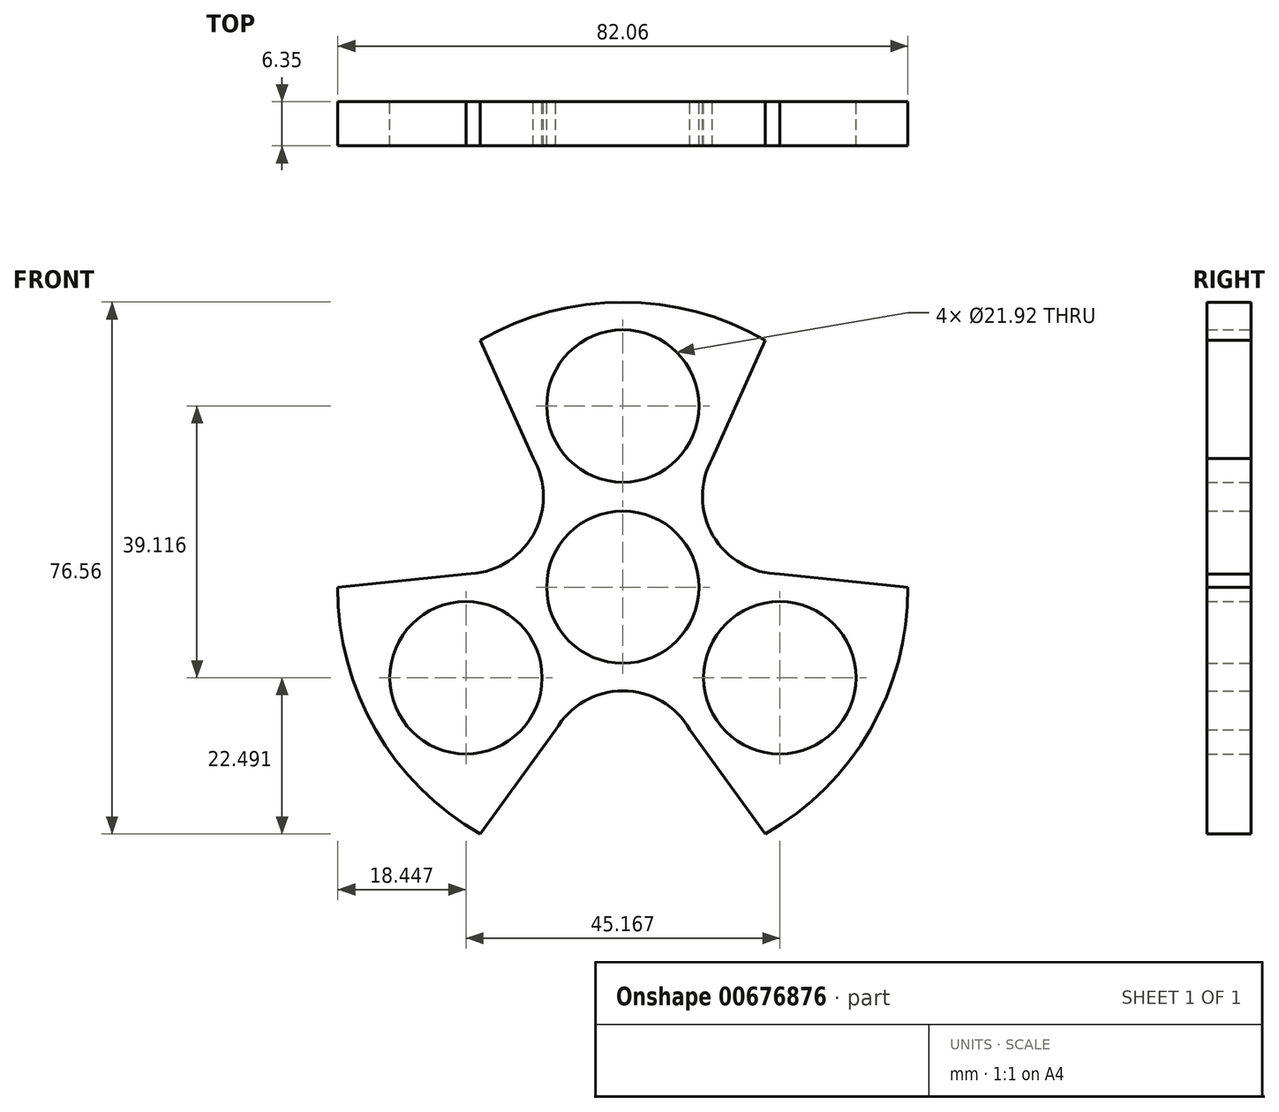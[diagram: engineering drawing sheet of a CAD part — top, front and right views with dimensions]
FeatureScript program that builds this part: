
annotation { "Feature Type Name" : "Feature", "Feature Type Description" : "" }
export const myFeature = defineFeature(function(context is Context, id is Id, definition is map)
    precondition{}
    {
        {
            var Q0;
            Q0=qCreatedBy(makeId("Front.planeOp"),FACE);
            var sketch = newSketch(context, id + "F0", { "sketchPlane" : qUnion([Q0])});
            skCircle(sketch, "E0", {"center": v(0, 0) * mm, "radius": 10.96 * mm});
            skCircle(sketch, "E1.cCircle", {"center": v(0, 0) * mm, "radius": 22.58 * mm, "construction": true});
            skPoint(sketch, "E1.0.midPoint", {"position": v(22.58, 0) * mm});
            skCircle(sketch, "E2", {"center": v(22.58, -13.04) * mm, "radius": 10.96 * mm});
            skPoint(sketch, "E2.perimeterSnap0", {"position": v(11.3, -19.56) * mm});
            skCircle(sketch, "E3", {"center": v(-22.58, -13.04) * mm, "radius": 10.96 * mm});
            skCircle(sketch, "E4", {"center": v(0, 26.08) * mm, "radius": 10.96 * mm});
            skArc(sketch, "E5", {"start": v(-22.58, 1.9) * mm, "mid": v(-12.94, 7.47) * mm, "end": v(-12.94, 18.6) * mm});
            skArc(sketch, "E6", {"start": v(12.9, 18.54) * mm, "mid": v(12.96, 7.43) * mm, "end": v(22.58, 1.9) * mm});
            skArc(sketch, "E7", {"start": v(9.65, -20.5) * mm, "mid": v(0, -14.94) * mm, "end": v(-9.65, -20.5) * mm});
            skCircle(sketch, "E8.cCircle", {"center": v(0, 0) * mm, "radius": 41.03 * mm, "construction": true});
            skLineSegment(sketch, "E8.0", {"start": v(41.03, 23.69) * mm, "end": v(41.03, -23.69) * mm, "construction": true});
            skLineSegment(sketch, "E8.1", {"start": v(41.03, -23.69) * mm, "end": v(0, -47.37) * mm, "construction": true});
            skLineSegment(sketch, "E8.2", {"start": v(0, -47.37) * mm, "end": v(-41.03, -23.69) * mm, "construction": true});
            skLineSegment(sketch, "E8.3", {"start": v(-41.03, -23.69) * mm, "end": v(-41.03, 23.69) * mm, "construction": true});
            skLineSegment(sketch, "E8.4", {"start": v(-41.03, 23.69) * mm, "end": v(0, 47.37) * mm, "construction": true});
            skLineSegment(sketch, "E8.5", {"start": v(0, 47.37) * mm, "end": v(20.51, 35.53) * mm, "construction": true});
            skPoint(sketch, "E8.0.midPoint", {"position": v(41.03, 0) * mm});
            skLineSegment(sketch, "E9", {"start": v(-12.94, 18.6) * mm, "end": v(-20.51, 35.53) * mm});
            skLineSegment(sketch, "E10", {"start": v(22.58, 1.9) * mm, "end": v(41.03, 0) * mm});
            skLineSegment(sketch, "E11", {"start": v(9.65, -20.5) * mm, "end": v(20.51, -35.53) * mm});
            skLineSegment(sketch, "E12", {"start": v(-9.65, -20.5) * mm, "end": v(-20.51, -35.53) * mm});
            skLineSegment(sketch, "E13", {"start": v(-22.58, 1.9) * mm, "end": v(-41.03, 0) * mm});
            skLineSegment(sketch, "E14", {"start": v(20.51, 35.53) * mm, "end": v(41.03, 23.69) * mm, "construction": true});
            skArc(sketch, "E15", {"start": v(20.51, 35.53) * mm, "mid": v(0, 41.03) * mm, "end": v(-20.51, 35.53) * mm});
            skArc(sketch, "E16", {"start": v(20.51, -35.53) * mm, "mid": v(35.58, -20.54) * mm, "end": v(41.03, 0) * mm});
            skArc(sketch, "E17", {"start": v(-41.03, 0) * mm, "mid": v(-35.58, -20.54) * mm, "end": v(-20.51, -35.53) * mm});
            skLineSegment(sketch, "E18", {"start": v(12.9, 18.54) * mm, "end": v(20.51, 35.53) * mm});
            skSolve(sketch);
        }
        {
            var Q0;
            Q0=makeQuery(id+"F0.imprint","IMPRINT",FACE,{"disambiguationData":[TD([[makeQuery(id+"F0.imprint","IMPRINT",EDGE,{"derivedFrom":sQuery(id+"F0.wireOp",EDGE,"E0")}),-1.0]])]});
            extrude(context, id + "F1", {"entities" : qUnion([Q0]), "depth" : 6.35 * mm, "offsetDistance" : 25.4 * mm});
        }
    });
